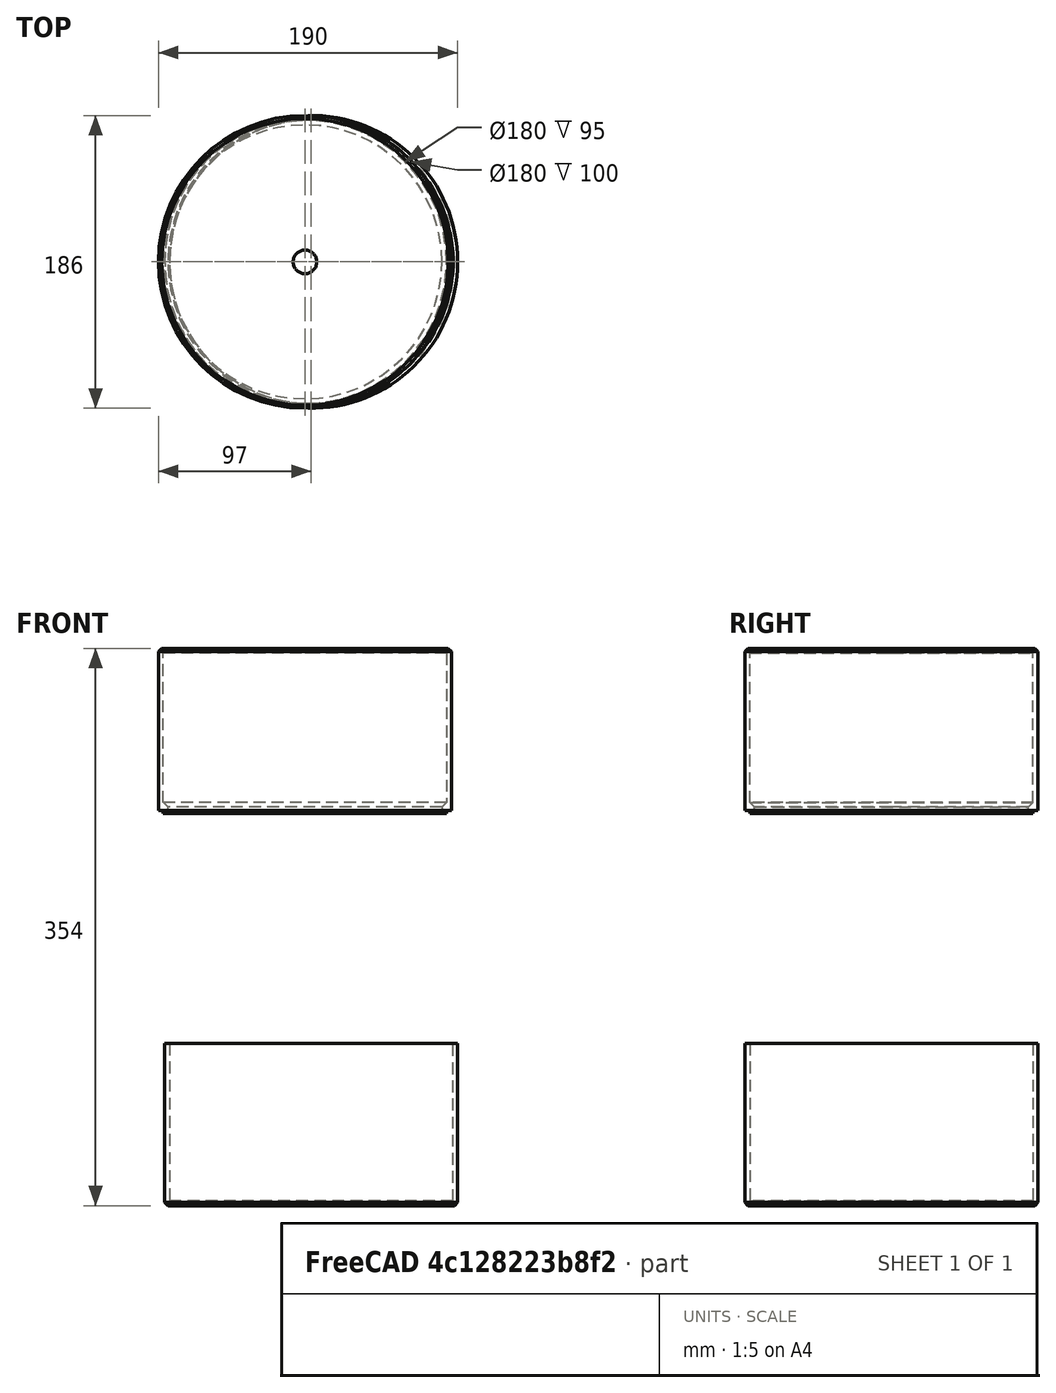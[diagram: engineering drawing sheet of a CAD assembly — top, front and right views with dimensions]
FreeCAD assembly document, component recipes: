
FREECAD ASSEMBLY — COMPONENT RECIPES ("CanHalves")

This assembly document has 2 components, labeled P0..P1 below (a component is one placed body or linked part). 2 of them carry a construction recipe — the FreeCAD feature program that regenerates the part from scratch, quoted from this document or its linked companion documents; the rest are supplied as boundary geometry only. No exploded tour is included for this assembly.
COMPONENT P0 — recipe-attached ("Bottom Body001", modeled in this document).
Construction recipe (the document's own serialized feature program — sketch geometry with constraints, then the solid features built on it; lengths are millimeters unless a unit is written):

FEATURE [PartDesign::AdditiveCylinder] Cylinder
  Angle = 360
  AttacherType = Attacher::AttachEngine3D
  Dimensions_Diameter = 180
  Dimensions_Height = 200
  Dimensions_Thickness = 3
  FirstAngle = 0
  Height = 103
  Radius = 93
  SecondAngle = 0
  Suppressed = false
  expr: Height = Dimensions_Height / 2 + Dimensions_Thickness
  expr: Radius = Dimensions_Diameter / 2 + Dimensions_Thickness
FEATURE [PartDesign::Thickness] Thickness
  Base = -> Cylinder [Face3]
  BaseFeature = -> Cylinder
  Intersection = false
  Join = 0
  Mode = 0
  Reversed = true
  SupportTransform = false
  Suppressed = false
  Value = 3
  expr: Value = <<Cylinder>>.Dimensions_Thickness
FEATURE [PartDesign::Chamfer] Chamfer001
  Angle = 45
  Base = -> Thickness [Edge2]
  BaseFeature = -> Thickness
  ChamferType = 0
  FlipDirection = false
  Size = 2
  Size2 = 1
  SupportTransform = false
  Suppressed = false
  UseAllEdges = false
FEATURE [PartDesign::Body] Body  label="Bottom Body"
  AllowCompound = false
  Group = -> [Cylinder,Thickness,Chamfer001]
  Origin = -> Origin
  Tip = -> Chamfer001
COMPONENT P1 — recipe-attached ("Top Body001", modeled in this document).
Construction recipe (the document's own serialized feature program — sketch geometry with constraints, then the solid features built on it; lengths are millimeters unless a unit is written):

FEATURE [PartDesign::FeatureBase] Clone
  BaseFeature = -> Thickness
  Suppressed = false
FEATURE [Sketcher::SketchObject] Sketch
  ArcFitTolerance = 1e-06
  AttachmentOffset = pos=(0,0,-5) rot=(0,0,1;0rad)
  AttachmentSupport = -> [Clone]
  ExternalGeometry = -> [Clone]
  FullyConstrained = true
  MakeInternals = false
  MapMode = 5
  Placement = pos=(0,0,98) rot=(0,0,1;0rad)
  expr: Constraints[3] = <<Cylinder>>.Dimensions_Thickness
  sketch-geometry (2):
    g0: Circle CenterX=0 CenterY=0 CenterZ=0 NormalX=0 NormalY=0 NormalZ=1 AngleXU=0 Radius=90
    g1: Circle CenterX=0 CenterY=0 CenterZ=0 NormalX=0 NormalY=0 NormalZ=1 AngleXU=0 Radius=87
  constraints (4):
    c: Coincident(g0,g-1)
    c: Equal(g0,g-3)
    c: Coincident(g1,g0)
    c: Distance(g1,g0) = 3
FEATURE [PartDesign::Pad] Pad
  BaseFeature = -> Clone
  Direction = (0,0,1)
  Length = 7
  Length2 = 10
  Profile = -> Sketch
  ReferenceAxis = -> Sketch [N_Axis]
  Suppressed = false
  Type = 0
FEATURE [PartDesign::Chamfer] Chamfer
  Angle = 45
  Base = -> Pad [Edge2]
  BaseFeature = -> Pad
  ChamferType = 0
  FlipDirection = false
  Size = 2
  Size2 = 1
  SupportTransform = false
  Suppressed = false
  UseAllEdges = false
FEATURE [PartDesign::Chamfer] Chamfer002
  Angle = 45
  Base = -> Chamfer [Edge11]
  BaseFeature = -> Chamfer
  ChamferType = 0
  FlipDirection = false
  Size = 2.9
  Size2 = 1
  SupportTransform = false
  Suppressed = false
  UseAllEdges = false
  expr: Size = <<Cylinder>>.Dimensions_Thickness - 0.1 mm
FEATURE [Sketcher::SketchObject] Sketch001
  ArcFitTolerance = 1e-06
  AttachmentSupport = -> [Chamfer002]
  FullyConstrained = true
  MakeInternals = false
  MapMode = 5
  Placement = pos=(0,0,0) rot=(1,0,0;3.14159rad)
  sketch-geometry (1):
    g0: Circle CenterX=0 CenterY=0 CenterZ=0 NormalX=0 NormalY=0 NormalZ=1 AngleXU=0 Radius=7.5
  constraints (2):
    c: Diameter(g0) = 15
    c: Coincident(g0,g-1)
FEATURE [PartDesign::Pocket] Pocket
  BaseFeature = -> Chamfer002
  Direction = (0,0,1)
  Length = 5
  Length2 = 5
  Profile = -> Sketch001
  ReferenceAxis = -> Sketch001 [N_Axis]
  Suppressed = false
  Type = 1
FEATURE [PartDesign::Body] Body001  label="Top Body"
  AllowCompound = false
  Group = -> [Clone,Sketch,Pad,Chamfer,Chamfer002,Sketch001,Pocket]
  Origin = -> Origin001
  Placement = pos=(-4,4.34e-14,354) rot=(1,0,0;3.14159rad)
  Tip = -> Pocket
PROVENANCE & LICENSES
A FreeCAD (.FCStd) document from a public repository crawl; recipes are the document's own serialized feature recipes (and, for linked parts, companion documents' recipes).
License: other.
